# Revit family: xxxPump_Commercial-Explosion_Proof-Zoeller-X180_X190_Non_Automatic_Series
name_source: partatom
category: Mechanical Equipment
units: mm (PartAtom-declared; Revit-internal decimal feet)

## family parameters
Always vertical = No
Cut with Voids When Loaded = No
OmniClass Number = 23.60.30.21
OmniClass Title = Pumps
Part Type = Normal
Room Calculation Point = No
Round Connector Dimension = Use Radius
Shared = Yes
Work Plane-Based = Yes

## types (23) — shared parameters
Assembly Code = D2010900
Cooling = Oil Filled
Cord Length = 240"
Cord Type = UL listed, 5-wire (1 Ph) or 8-wire (3 Ph) SOOW
Default Elevation = 0"
Description = High Head Flow-Mate Effluent Pump For Hazardous Enviroments
Discharge Diameter = 1-1/2" NPT (optional 2" or 3" flange available)
Discharge Height = 6 1/16"
Discharge Radius = 3/4"
Gasket = Neoprene square rings
Hardware = Stainless Steel or Brass
Hertz = 60
Impeller = Bronze
Impeller Type = Non-clogging vortex
Installation Type = Floor Mounted
Length = 13 5/16"
Lower Bearing = Ball Bearing
Manufacturer = Zoeller
Material = Cast Iron-Zoeller-Powder Coated Epoxy
Max. Operating Temp. = 104° F (40° C)
Mechanical Seals = Carbon and ceramic with stainless steel parts
Motor Protection = Auto reset thermal overload (1Ph) or thermal sensor (3Ph).
Motor Shaft = 416 Stainless Steel
Motor Type = Submersible
Operation = nonautomatic
Overall Height = 23 9/32"
Price = Prices may vary. Please consult Manufacturer Representative for most up-to-date price list.
Product Documentation Link = https://www.zoellerpumps.com
Product Page URL = https://www.zoellerpumps.com
RPM = 3450
Revised Date = 03/01/2023
Solid Handling = 3/4" (19 mm) Spherical Solids
Type = Permanent Split Capacitor or 3 Ph
URL = http://www.zoellerpumps.com
Upper Bearing = Ball Bearing
Warranty Information = 36 Months (Limited)
Waste Connection = Yes
Weight = 126 Lbs
Width = 9 1/8"

## per-type parameters (varying)
| type | Amps | Apparent Load | Insulation | Max. Flow @ 30' | Max. Flow @ 5' | Maximum Head | Model | Motor | Phase | Voltage |
| EX188 230V/1Ph/14.0A/1-1/2HP | 14 A | 3220 VA | Class F | 116 GPM | 145 GPM | 91 ft. (28 m) | X188 | 1.5 HP | 1 | 230 V |
| IX188 200-208V/1Ph/16.8A/1-1/2HP | 17 A | 3360 VA | Class F | 116 GPM | 145 GPM | 91 ft. (28 m) | X188 | 1.5 HP | 1 | 200 V |
| FX188 230V/3Ph/8.9A/1-1/2HP | 9 A | 2047 VA | Class F | 116 GPM | 145 GPM | 91 ft. (28 m) | X188 | 1.5 HP | 3 | 230 V |
| JX188 200-208V/3Ph/10.3A/1-1/2HP | 10 A | 2060 VA | Class F | 116 GPM | 145 GPM | 91 ft. (28 m) | JX188 | 1.5 HP | 3 | 200 V |
| GX188 460V/3Ph/4.6A/1-1/2HP | 5 A | 2116 VA | Class F | 116 GPM | 145 GPM | 91 ft. (28 m) | X188 | 1.5 HP | 3 | 460 V |
| BAX188 575V/3Ph/3.5A/1-1/2HP | 4 A | 2013 VA | Class F | 116 GPM | 145 GPM | 91 ft. (28 m) | X188 | 1.5 HP | 3 | 575 V |
| EX189 230V/1Ph/17.1A/2HP | 17 A | 3933 VA | Class F | 120 GPM | 145 GPM | 110 ft. (34 m) | EX189 | 2 HP | 1 | 230 V |
| IX189 200-208V/1Ph/20.5A/2HP | 21 A | 4100 VA | Class F | 120 GPM | 145 GPM | 110 ft. (34 m) | IX189 | 2 HP | 1 | 200 V |
| FX189 230V/3Ph/11.2A/2HP | 11 A | 2576 VA | Class F | 120 GPM | 145 GPM | 110 ft. (34 m) | FX189 | 2 HP | 3 | 230 V |
| JX189 200-208V/3Ph/13.2A/2HP | 13 A | 2640 VA | Class F | 120 GPM | 145 GPM | 110 ft. (34 m) | JX189 | 2 HP | 3 | 200 V |
| GX189 460V/3Ph/6.0A/2HP | 6 A | 2760 VA | Class F | 120 GPM | 145 GPM | 110 ft. (34 m) | GX189 | 2 HP | 3 | 460 V |
| BAX189 575V/3Ph/5.8A/2HP | 6 A | 3335 VA | Class F | 120 GPM | 145 GPM | 110 ft. (34 m) | BAX189 | 2 HP | 3 | 575 V |
| EX191 230V/1Ph/14.5A/2HP | 15 A | 3335 VA | Class F | 45 GPM | 45 GPM | 137 ft. (42 m) | EX191 | 2 HP | 1 | 230 V |
| EX186 230V/1Ph/13.7A/1-1/2HP | 14 A | 3151 VA | Class F | 58 GPM | 58 GPM | 114 ft. (35 m) | EX186 | 1.5 HP | 1 | 230 V |
| IX186 200-208V/1Ph/17.2A/1-1/2HP | 17 A | 3440 VA | Class F | 58 GPM | 58 GPM | 114 ft. (35 m) | IX186 | 1.5 HP | 1 | 200 V |
| FX186 230V/3Ph/9.2A/1-1/2HP | 9 A | 2116 VA | Class F | 58 GPM | 58 GPM | 114 ft. (35 m) | FX186 | 1.5 HP | 3 | 230 V |
| JX186 200-208V/3Ph/10.3A/1-1/2HP | 10 A | 2060 VA | Class F | 58 GPM | 58 GPM | 114 ft. (35 m) | JX186 | 1.5 HP | 3 | 200 V |
| GX186 460V/3Ph/4.6A/1-1/2HP | 5 A | 2116 VA | Class F | 58 GPM | 58 GPM | 114 ft. (35 m) | GX186 | 1.5 HP | 3 | 460 V |
| EX185 230V/1Ph/9.8A/1HP | 10 A | 2254 VA | Class B | 85 GPM | 0 GPM | 73 ft. (22 m) | EX185 | 1 HP | 1 | 230 V |
| IX185 200-208V/1Ph/11.5A/1HP | 12 A | 2300 VA | Class B | 85 GPM | 0 GPM | 73 ft. (22 m) | IX185 | 1 HP | 1 | 200 V |
| FX185 230V/3Ph/7.4A/1HP | 7 A | 1702 VA | Class B | 85 GPM | 0 GPM | 73 ft. (22 m) | FX185 | 1 HP | 3 | 230 V |
| JX185 200-208V/3Ph/7.5A/1HP | 8 A | 1500 VA | Class B | 85 GPM | 0 GPM | 73 ft. (22 m) | JX185 | 1 HP | 3 | 200 V |
| GX185 460V/3Ph/3.7A/1HP | 4 A | 1702 VA | Class B | 85 GPM | 0 GPM | 73 ft. (22 m) | GX185 | 1 HP | 3 | 460 V |

## geometry (parser evidence)
native form markers: Sweep x3
no freeform markers — native parametric forms only
